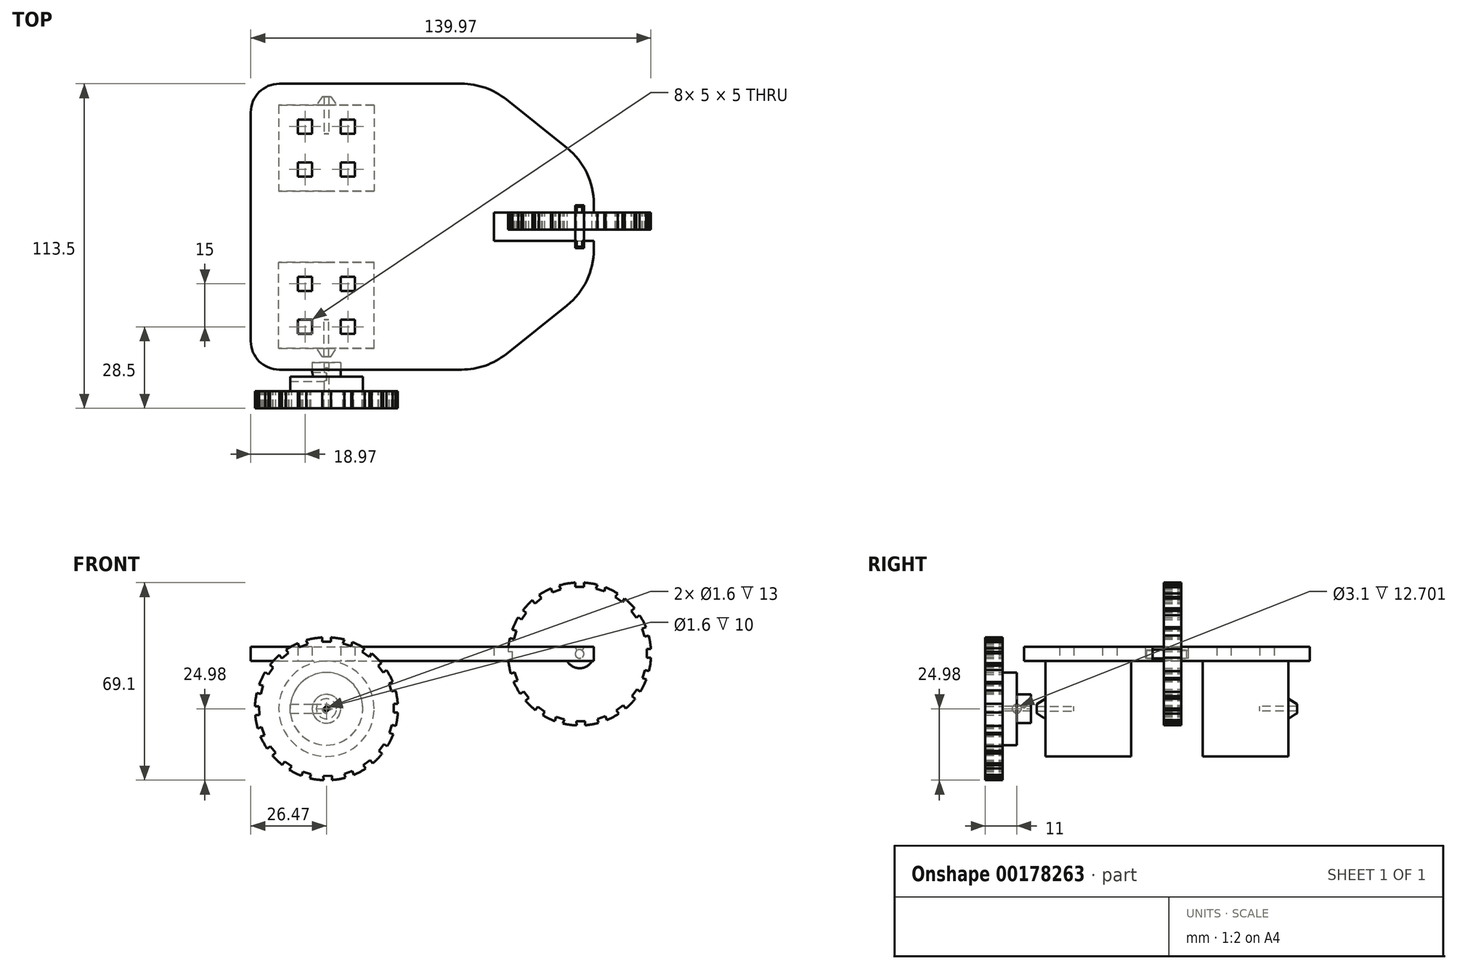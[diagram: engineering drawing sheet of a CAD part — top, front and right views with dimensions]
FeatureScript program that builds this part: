
annotation { "Feature Type Name" : "Feature", "Feature Type Description" : "" }
export const myFeature = defineFeature(function(context is Context, id is Id, definition is map)
    precondition{}
    {
        {
            var Q0;
            Q0=qCreatedBy(makeId("Front.planeOp"),FACE);
            var sketch = newSketch(context, id + "F0", { "sketchPlane" : qUnion([Q0])});
            skCircle(sketch, "E0", {"center": v(0, 0) * mm, "radius": 16.67 * mm});
            skCircle(sketch, "E1", {"center": v(0, 0) * mm, "radius": 0.8 * mm});
            skSolve(sketch);
        }
        {
            var Q0;
            Q0=makeQuery(id+"F0.imprint","IMPRINT",FACE,{"disambiguationData":[TD([[makeQuery(id+"F0.imprint","IMPRINT",EDGE,{"derivedFrom":sQuery(id+"F0.wireOp",EDGE,"E0")}),1.0]])]});
            var Q1;
            Q1=sQuery(id+"F0.wireOp",EDGE,"E0");
            extrude(context, id + "F1", {"entities" : qUnion([Q0]), "surfaceEntities" : qUnion([Q1]), "depth" : 30 * mm});
        }
        {
            var Q0;
            Q0=makeQuery(id+"F0.imprint","IMPRINT",FACE,{"disambiguationData":[TD([[makeQuery(id+"F0.imprint","IMPRINT",EDGE,{"derivedFrom":sQuery(id+"F0.wireOp",EDGE,"E1")}),1.0]])]});
            var Q1;
            Q1=sQuery(id+"F0.wireOp",EDGE,"E1");
            extrude(context, id + "F2", {"entities" : qUnion([Q0]), "surfaceEntities" : qUnion([Q1]), "depth" : 45 * mm});
        }
        {
            var Q0;
            Q0=qCreatedBy(makeId("Front.planeOp"),FACE);
            cPlane(context, id + "F3", {"entities" : qUnion([Q0]), "cplaneType" : CPlaneType.OFFSET, "offset" : 30 * mm, "width" : 150 * mm, "height" : 150 * mm});
        }
        {
            var Q0;
            Q0=qCreatedBy(id+"F3.planeOp",FACE);
            var sketch = newSketch(context, id + "F4", { "sketchPlane" : qUnion([Q0])});
            skCircle(sketch, "E2", {"center": v(0, 0) * mm, "radius": 3.5 * mm});
            skSolve(sketch);
        }
        {
            var Q0;
            Q0 = qSketchRegion(id + "F4", true);
            extrude(context, id + "F5", {"entities" : qUnion([Q0]), "operationType" : NewBodyOperationType.ADD, "depth" : 3 * mm, "hasDraft" : true, "draftAngle" : 33 * degree, "draftPullDirection" : true});
        }
        {
            var Q0;
            Q0=qCreatedBy(makeId("Front.planeOp"),FACE);
            cPlane(context, id + "F6", {"entities" : qUnion([Q0]), "cplaneType" : CPlaneType.OFFSET, "offset" : 45 * mm, "width" : 150 * mm, "height" : 150 * mm});
        }
        {
            var Q0;
            Q0=qCreatedBy(id+"F6.planeOp",FACE);
            var sketch = newSketch(context, id + "F7", { "sketchPlane" : qUnion([Q0])});
            skCircle(sketch, "E3", {"center": v(0, 0) * mm, "radius": 12.7 * mm});
            skCircle(sketch, "E4", {"center": v(0, 0) * mm, "radius": 2.75 * mm});
            skCircle(sketch, "E5", {"center": v(0, 0) * mm, "radius": 0.8 * mm});
            skSolve(sketch);
        }
        {
            var Q0;
            Q0=makeQuery(id+"F7.imprint","IMPRINT",FACE,{"disambiguationData":[TD([[makeQuery(id+"F7.imprint","IMPRINT",EDGE,{"derivedFrom":sQuery(id+"F7.wireOp",EDGE,"E4")}),1.0]])]});
            extrude(context, id + "F8", {"entities" : qUnion([Q0]), "oppositeDirection" : true, "depth" : 10 * mm});
        }
        {
            var Q0;
            Q0 = qSketchRegion(id + "F7", true);
            extrude(context, id + "F9", {"entities" : qUnion([Q0]), "operationType" : NewBodyOperationType.ADD, "oppositeDirection" : true, "depth" : 5 * mm});
        }
        {
            var Q0;
            Q0=makeQuery(id+"F7.imprint","IMPRINT",FACE,{"disambiguationData":[TD([[makeQuery(id+"F7.imprint","IMPRINT",EDGE,{"derivedFrom":sQuery(id+"F7.wireOp",EDGE,"E5")}),1.0]])]});
            var Q1;
            Q1=sQuery(id+"F7.wireOp",EDGE,"E5");
            extrude(context, id + "F10", {"entities" : qUnion([Q0]), "operationType" : NewBodyOperationType.REMOVE, "surfaceEntities" : qUnion([Q1]), "depth" : 25 * mm, "hasSecondDirection" : true, "secondDirectionOppositeDirection" : true, "secondDirectionDepth" : 25 * mm});
        }
        {
            var Q0;
            Q0=qCreatedBy(makeId("Top.planeOp"),FACE);
            var sketch = newSketch(context, id + "F11", { "sketchPlane" : qUnion([Q0])});
            skLineSegment(sketch, "E6", {"start": v(0, 0) * mm, "end": v(0, -37.5) * mm});
            skLineSegment(sketch, "E7", {"start": v(19.12, -37.5) * mm, "end": v(-21.18, -37.5) * mm});
            skCircle(sketch, "E8", {"center": v(0, -37.5) * mm, "radius": 0.75 * mm});
            skSolve(sketch);
        }
        {
            var Q0;
            Q0 = qSketchRegion(id + "F11", true);
            extrude(context, id + "F12", {"entities" : qUnion([Q0]), "operationType" : NewBodyOperationType.REMOVE, "depth" : 25 * mm});
        }
        {
            var Q0;
            Q0=qCreatedBy(id+"F6.planeOp",FACE);
            var sketch = newSketch(context, id + "F13", { "sketchPlane" : qUnion([Q0])});
            skCircle(sketch, "E9", {"center": v(0, 0) * mm, "radius": 25 * mm});
            skLineSegment(sketch, "E10.bottom", {"start": v(0, 25) * mm, "end": v(1.5, 25) * mm});
            skLineSegment(sketch, "E10.top", {"start": v(0, 23.5) * mm, "end": v(1.5, 23.5) * mm});
            skLineSegment(sketch, "E10.right", {"start": v(1.5, 25) * mm, "end": v(1.5, 23.5) * mm});
            skLineSegment(sketch, "E11.MirrorCS", {"start": v(0, 25) * mm, "end": v(-1.5, 25) * mm});
            skLineSegment(sketch, "E12.MirrorCS", {"start": v(-1.5, 25) * mm, "end": v(-1.5, 23.5) * mm});
            skLineSegment(sketch, "E13.MirrorCS", {"start": v(0, 23.5) * mm, "end": v(-1.5, 23.5) * mm});
            skLineSegment(sketch, "E14.1.0", {"start": v(6.25, 24.25) * mm, "end": v(5.8, 22.82) * mm});
            skLineSegment(sketch, "E14.1.1", {"start": v(7.68, 23.8) * mm, "end": v(6.25, 24.25) * mm});
            skLineSegment(sketch, "E14.1.2", {"start": v(7.68, 23.8) * mm, "end": v(9.1, 23.33) * mm});
            skLineSegment(sketch, "E14.1.3", {"start": v(9.1, 23.33) * mm, "end": v(8.65, 21.9) * mm});
            skLineSegment(sketch, "E14.1.4", {"start": v(7.22, 22.36) * mm, "end": v(8.65, 21.9) * mm});
            skLineSegment(sketch, "E14.1.5", {"start": v(7.22, 22.36) * mm, "end": v(5.8, 22.82) * mm});
            skLineSegment(sketch, "E14.2.0", {"start": v(13.4, 21.16) * mm, "end": v(12.53, 19.94) * mm});
            skLineSegment(sketch, "E14.2.1", {"start": v(14.62, 20.28) * mm, "end": v(13.4, 21.16) * mm});
            skLineSegment(sketch, "E14.2.2", {"start": v(14.62, 20.28) * mm, "end": v(15.84, 19.4) * mm});
            skLineSegment(sketch, "E14.2.3", {"start": v(15.84, 19.4) * mm, "end": v(14.96, 18.19) * mm});
            skLineSegment(sketch, "E14.2.4", {"start": v(13.74, 19.06) * mm, "end": v(14.96, 18.19) * mm});
            skLineSegment(sketch, "E14.2.5", {"start": v(13.74, 19.06) * mm, "end": v(12.53, 19.94) * mm});
            skLineSegment(sketch, "E14.3.0", {"start": v(19.26, 16.01) * mm, "end": v(18.05, 15.13) * mm});
            skLineSegment(sketch, "E14.3.1", {"start": v(20.14, 14.8) * mm, "end": v(19.26, 16.01) * mm});
            skLineSegment(sketch, "E14.3.2", {"start": v(20.14, 14.8) * mm, "end": v(21.03, 13.6) * mm});
            skLineSegment(sketch, "E14.3.3", {"start": v(21.03, 13.6) * mm, "end": v(19.82, 12.7) * mm});
            skLineSegment(sketch, "E14.3.4", {"start": v(18.94, 13.92) * mm, "end": v(19.82, 12.7) * mm});
            skLineSegment(sketch, "E14.3.5", {"start": v(18.94, 13.92) * mm, "end": v(18.05, 15.13) * mm});
            skLineSegment(sketch, "E14.4.0", {"start": v(23.25, 9.32) * mm, "end": v(21.82, 8.85) * mm});
            skLineSegment(sketch, "E14.4.1", {"start": v(23.72, 7.9) * mm, "end": v(23.25, 9.32) * mm});
            skLineSegment(sketch, "E14.4.2", {"start": v(23.72, 7.9) * mm, "end": v(24.2, 6.48) * mm});
            skLineSegment(sketch, "E14.4.3", {"start": v(24.2, 6.48) * mm, "end": v(22.77, 6) * mm});
            skLineSegment(sketch, "E14.4.4", {"start": v(22.3, 7.43) * mm, "end": v(22.77, 6) * mm});
            skLineSegment(sketch, "E14.4.5", {"start": v(22.3, 7.43) * mm, "end": v(21.82, 8.85) * mm});
            skLineSegment(sketch, "E14.5.0", {"start": v(24.99, 1.73) * mm, "end": v(23.49, 1.72) * mm});
            skLineSegment(sketch, "E14.5.1", {"start": v(25, 0.23) * mm, "end": v(24.99, 1.73) * mm});
            skLineSegment(sketch, "E14.5.2", {"start": v(25, 0.23) * mm, "end": v(25.01, -1.27) * mm});
            skLineSegment(sketch, "E14.5.3", {"start": v(25.01, -1.27) * mm, "end": v(23.51, -1.28) * mm});
            skLineSegment(sketch, "E14.5.4", {"start": v(23.5, 0.22) * mm, "end": v(23.51, -1.28) * mm});
            skLineSegment(sketch, "E14.5.5", {"start": v(23.5, 0.22) * mm, "end": v(23.49, 1.72) * mm});
            skLineSegment(sketch, "E14.6.0", {"start": v(24.3, -6.03) * mm, "end": v(22.88, -5.58) * mm});
            skLineSegment(sketch, "E14.6.1", {"start": v(23.86, -7.46) * mm, "end": v(24.3, -6.03) * mm});
            skLineSegment(sketch, "E14.6.2", {"start": v(23.86, -7.46) * mm, "end": v(23.41, -8.9) * mm});
            skLineSegment(sketch, "E14.6.3", {"start": v(23.41, -8.9) * mm, "end": v(21.98, -8.45) * mm});
            skLineSegment(sketch, "E14.6.4", {"start": v(22.43, -7.02) * mm, "end": v(21.98, -8.45) * mm});
            skLineSegment(sketch, "E14.6.5", {"start": v(22.43, -7.02) * mm, "end": v(22.88, -5.58) * mm});
            skLineSegment(sketch, "E14.7.0", {"start": v(21.28, -13.2) * mm, "end": v(20.05, -12.34) * mm});
            skLineSegment(sketch, "E14.7.1", {"start": v(20.41, -14.43) * mm, "end": v(21.28, -13.2) * mm});
            skLineSegment(sketch, "E14.7.2", {"start": v(20.41, -14.43) * mm, "end": v(19.55, -15.66) * mm});
            skLineSegment(sketch, "E14.7.3", {"start": v(19.55, -15.66) * mm, "end": v(18.32, -14.8) * mm});
            skLineSegment(sketch, "E14.7.4", {"start": v(19.19, -13.57) * mm, "end": v(18.32, -14.8) * mm});
            skLineSegment(sketch, "E14.7.5", {"start": v(19.19, -13.57) * mm, "end": v(20.05, -12.34) * mm});
            skLineSegment(sketch, "E14.8.0", {"start": v(16.2, -19.1) * mm, "end": v(15.3, -17.9) * mm});
            skLineSegment(sketch, "E14.8.1", {"start": v(15, -20) * mm, "end": v(16.2, -19.1) * mm});
            skLineSegment(sketch, "E14.8.2", {"start": v(15, -20) * mm, "end": v(13.79, -20.9) * mm});
            skLineSegment(sketch, "E14.8.3", {"start": v(13.79, -20.9) * mm, "end": v(12.9, -19.7) * mm});
            skLineSegment(sketch, "E14.8.4", {"start": v(14.1, -18.8) * mm, "end": v(12.9, -19.7) * mm});
            skLineSegment(sketch, "E14.8.5", {"start": v(14.1, -18.8) * mm, "end": v(15.3, -17.9) * mm});
            skLineSegment(sketch, "E14.9.0", {"start": v(9.54, -23.16) * mm, "end": v(9.05, -21.74) * mm});
            skLineSegment(sketch, "E14.9.1", {"start": v(8.12, -23.65) * mm, "end": v(9.54, -23.16) * mm});
            skLineSegment(sketch, "E14.9.2", {"start": v(8.12, -23.65) * mm, "end": v(6.7, -24.13) * mm});
            skLineSegment(sketch, "E14.9.3", {"start": v(6.7, -24.13) * mm, "end": v(6.21, -22.71) * mm});
            skLineSegment(sketch, "E14.9.4", {"start": v(7.63, -22.23) * mm, "end": v(6.21, -22.71) * mm});
            skLineSegment(sketch, "E14.9.5", {"start": v(7.63, -22.23) * mm, "end": v(9.05, -21.74) * mm});
            skLineSegment(sketch, "E14.10.0", {"start": v(1.96, -24.97) * mm, "end": v(1.93, -23.47) * mm});
            skLineSegment(sketch, "E14.10.1", {"start": v(0.46, -25) * mm, "end": v(1.96, -24.97) * mm});
            skLineSegment(sketch, "E14.10.2", {"start": v(0.46, -25) * mm, "end": v(-1.04, -25.02) * mm});
            skLineSegment(sketch, "E14.10.3", {"start": v(-1.04, -25.02) * mm, "end": v(-1.07, -23.52) * mm});
            skLineSegment(sketch, "E14.10.4", {"start": v(0.43, -23.5) * mm, "end": v(-1.07, -23.52) * mm});
            skLineSegment(sketch, "E14.10.5", {"start": v(0.43, -23.5) * mm, "end": v(1.93, -23.47) * mm});
            skLineSegment(sketch, "E14.11.0", {"start": v(-5.8, -24.36) * mm, "end": v(-5.37, -22.93) * mm});
            skLineSegment(sketch, "E14.11.1", {"start": v(-7.24, -23.93) * mm, "end": v(-5.8, -24.36) * mm});
            skLineSegment(sketch, "E14.11.2", {"start": v(-7.24, -23.93) * mm, "end": v(-8.68, -23.5) * mm});
            skLineSegment(sketch, "E14.11.3", {"start": v(-8.68, -23.5) * mm, "end": v(-8.24, -22.06) * mm});
            skLineSegment(sketch, "E14.11.4", {"start": v(-6.8, -22.5) * mm, "end": v(-8.24, -22.06) * mm});
            skLineSegment(sketch, "E14.11.5", {"start": v(-6.8, -22.5) * mm, "end": v(-5.37, -22.93) * mm});
            skLineSegment(sketch, "E14.12.0", {"start": v(-13.01, -21.4) * mm, "end": v(-12.16, -20.17) * mm});
            skLineSegment(sketch, "E14.12.1", {"start": v(-14.25, -20.54) * mm, "end": v(-13.01, -21.4) * mm});
            skLineSegment(sketch, "E14.12.2", {"start": v(-14.25, -20.54) * mm, "end": v(-15.48, -19.69) * mm});
            skLineSegment(sketch, "E14.12.3", {"start": v(-15.48, -19.69) * mm, "end": v(-14.62, -18.46) * mm});
            skLineSegment(sketch, "E14.12.4", {"start": v(-13.4, -19.31) * mm, "end": v(-14.62, -18.46) * mm});
            skLineSegment(sketch, "E14.12.5", {"start": v(-13.4, -19.31) * mm, "end": v(-12.16, -20.17) * mm});
            skLineSegment(sketch, "E14.13.0", {"start": v(-18.96, -16.37) * mm, "end": v(-17.77, -15.46) * mm});
            skLineSegment(sketch, "E14.13.1", {"start": v(-19.87, -15.17) * mm, "end": v(-18.96, -16.37) * mm});
            skLineSegment(sketch, "E14.13.2", {"start": v(-19.87, -15.17) * mm, "end": v(-20.78, -13.98) * mm});
            skLineSegment(sketch, "E14.13.3", {"start": v(-20.78, -13.98) * mm, "end": v(-19.59, -13.07) * mm});
            skLineSegment(sketch, "E14.13.4", {"start": v(-18.68, -14.26) * mm, "end": v(-19.59, -13.07) * mm});
            skLineSegment(sketch, "E14.13.5", {"start": v(-18.68, -14.26) * mm, "end": v(-17.77, -15.46) * mm});
            skLineSegment(sketch, "E14.14.0", {"start": v(-23.07, -9.75) * mm, "end": v(-21.66, -9.25) * mm});
            skLineSegment(sketch, "E14.14.1", {"start": v(-23.57, -8.33) * mm, "end": v(-23.07, -9.75) * mm});
            skLineSegment(sketch, "E14.14.2", {"start": v(-23.57, -8.33) * mm, "end": v(-24.07, -6.92) * mm});
            skLineSegment(sketch, "E14.14.3", {"start": v(-24.07, -6.92) * mm, "end": v(-22.66, -6.42) * mm});
            skLineSegment(sketch, "E14.14.4", {"start": v(-22.16, -7.83) * mm, "end": v(-22.66, -6.42) * mm});
            skLineSegment(sketch, "E14.14.5", {"start": v(-22.16, -7.83) * mm, "end": v(-21.66, -9.25) * mm});
            skLineSegment(sketch, "E14.15.0", {"start": v(-24.95, -2.19) * mm, "end": v(-23.45, -2.15) * mm});
            skLineSegment(sketch, "E14.15.1", {"start": v(-25, -0.69) * mm, "end": v(-24.95, -2.19) * mm});
            skLineSegment(sketch, "E14.15.2", {"start": v(-25, -0.69) * mm, "end": v(-25.03, 0.81) * mm});
            skLineSegment(sketch, "E14.15.3", {"start": v(-25.03, 0.81) * mm, "end": v(-23.53, 0.85) * mm});
            skLineSegment(sketch, "E14.15.4", {"start": v(-23.5, -0.65) * mm, "end": v(-23.53, 0.85) * mm});
            skLineSegment(sketch, "E14.15.5", {"start": v(-23.5, -0.65) * mm, "end": v(-23.45, -2.15) * mm});
            skLineSegment(sketch, "E14.16.0", {"start": v(-24.41, 5.58) * mm, "end": v(-22.98, 5.16) * mm});
            skLineSegment(sketch, "E14.16.1", {"start": v(-24, 7.02) * mm, "end": v(-24.41, 5.58) * mm});
            skLineSegment(sketch, "E14.16.2", {"start": v(-24, 7.02) * mm, "end": v(-23.57, 8.46) * mm});
            skLineSegment(sketch, "E14.16.3", {"start": v(-23.57, 8.46) * mm, "end": v(-22.13, 8.04) * mm});
            skLineSegment(sketch, "E14.16.4", {"start": v(-22.55, 6.6) * mm, "end": v(-22.13, 8.04) * mm});
            skLineSegment(sketch, "E14.16.5", {"start": v(-22.55, 6.6) * mm, "end": v(-22.98, 5.16) * mm});
            skLineSegment(sketch, "E14.17.0", {"start": v(-21.52, 12.82) * mm, "end": v(-20.28, 11.97) * mm});
            skLineSegment(sketch, "E14.17.1", {"start": v(-20.67, 14.06) * mm, "end": v(-21.52, 12.82) * mm});
            skLineSegment(sketch, "E14.17.2", {"start": v(-20.67, 14.06) * mm, "end": v(-19.83, 15.3) * mm});
            skLineSegment(sketch, "E14.17.3", {"start": v(-19.83, 15.3) * mm, "end": v(-18.6, 14.45) * mm});
            skLineSegment(sketch, "E14.17.4", {"start": v(-19.43, 13.21) * mm, "end": v(-18.6, 14.45) * mm});
            skLineSegment(sketch, "E14.17.5", {"start": v(-19.43, 13.21) * mm, "end": v(-20.28, 11.97) * mm});
            skLineSegment(sketch, "E14.18.0", {"start": v(-16.54, 18.8) * mm, "end": v(-15.62, 17.62) * mm});
            skLineSegment(sketch, "E14.18.1", {"start": v(-15.36, 19.73) * mm, "end": v(-16.54, 18.8) * mm});
            skLineSegment(sketch, "E14.18.2", {"start": v(-15.36, 19.73) * mm, "end": v(-14.17, 20.65) * mm});
            skLineSegment(sketch, "E14.18.3", {"start": v(-14.17, 20.65) * mm, "end": v(-13.25, 19.47) * mm});
            skLineSegment(sketch, "E14.18.4", {"start": v(-14.43, 18.54) * mm, "end": v(-13.25, 19.47) * mm});
            skLineSegment(sketch, "E14.18.5", {"start": v(-14.43, 18.54) * mm, "end": v(-15.62, 17.62) * mm});
            skLineSegment(sketch, "E14.19.0", {"start": v(-9.96, 22.98) * mm, "end": v(-9.45, 21.57) * mm});
            skLineSegment(sketch, "E14.19.1", {"start": v(-8.55, 23.5) * mm, "end": v(-9.96, 22.98) * mm});
            skLineSegment(sketch, "E14.19.2", {"start": v(-8.55, 23.5) * mm, "end": v(-7.14, 24) * mm});
            skLineSegment(sketch, "E14.19.3", {"start": v(-7.14, 24) * mm, "end": v(-6.63, 22.6) * mm});
            skLineSegment(sketch, "E14.19.4", {"start": v(-8.04, 22.08) * mm, "end": v(-6.63, 22.6) * mm});
            skLineSegment(sketch, "E14.19.5", {"start": v(-8.04, 22.08) * mm, "end": v(-9.45, 21.57) * mm});
            skLineSegment(sketch, "E14.anchor1", {"start": v(0, 0) * mm, "end": v(-1.5, 23.5) * mm, "construction": true});
            skLineSegment(sketch, "E14.anchor2", {"start": v(0, 0) * mm, "end": v(-9.45, 21.57) * mm, "construction": true});
            skCircle(sketch, "E15", {"center": v(0, 0) * mm, "radius": 0.82 * mm});
            skCircle(sketch, "E16", {"center": v(0, 0) * mm, "radius": 5 * mm});
            skSolve(sketch);
        }
        {
            var Q0;
            {var subQ37=sQuery(id+"F13.wireOp",EDGE,"E10.top");Q0=makeQuery(id+"F13.imprint","IMPRINT",FACE,{"disambiguationData":[TD([[makeQuery(id+"F13.imprint","IMPRINT",EDGE,{"derivedFrom":subQ37}),-1.0]])]});}
            var Q1;
            Q1=makeQuery(id+"F13.imprint","IMPRINT",FACE,{"disambiguationData":[TD([[makeQuery(id+"F13.imprint","IMPRINT",EDGE,{"derivedFrom":sQuery(id+"F13.wireOp",EDGE,"E15")}),-1.0]])]});
            extrude(context, id + "F14", {"entities" : qUnion([Q0, Q1]), "operationType" : NewBodyOperationType.ADD, "depth" : 6 * mm});
        }
        {
            var Q0;
            Q0=makeQuery(id+"F13.imprint","IMPRINT",FACE,{"disambiguationData":[TD([[makeQuery(id+"F13.imprint","IMPRINT",EDGE,{"derivedFrom":sQuery(id+"F13.wireOp",EDGE,"E15")}),-1.0]])]});
            extrude(context, id + "F15", {"entities" : qUnion([Q0]), "operationType" : NewBodyOperationType.ADD, "oppositeDirection" : true, "depth" : 10 * mm});
        }
        {
            var Q0;
            Q0=qCreatedBy(makeId("Right.planeOp"),FACE);
            var sketch = newSketch(context, id + "F16", { "sketchPlane" : qUnion([Q0])});
            skLineSegment(sketch, "E17", {"start": v(-35, 0) * mm, "end": v(-35, 17.32) * mm});
            skLineSegment(sketch, "E18.0", {"start": v(-40, 0) * mm, "end": v(-40, 17.32) * mm});
            skCircle(sketch, "E19", {"center": v(-40, 0) * mm, "radius": 1.55 * mm});
            skSolve(sketch);
        }
        {
            var Q0;
            Q0=makeQuery(id+"F16.imprint","IMPRINT",FACE,{"disambiguationData":[TD([[makeQuery(id+"F16.imprint","IMPRINT",EDGE,{"derivedFrom":sQuery(id+"F16.wireOp",EDGE,"E19")}),1.0]])]});
            extrude(context, id + "F17", {"entities" : qUnion([Q0]), "operationType" : NewBodyOperationType.REMOVE, "oppositeDirection" : true, "depth" : 25 * mm});
        }
        {
            var Q0;
            Q0=qCreatedBy(makeId("Front.planeOp"),FACE);
            cPlane(context, id + "F18", {"entities" : qUnion([Q0]), "cplaneType" : CPlaneType.OFFSET, "offset" : 12.5 * mm, "oppositeDirection" : true, "width" : 150 * mm, "height" : 150 * mm});
        }
        {
            var Q0;
            Q0=makeQuery(id+"F1.opExtrude","SWEPT_BODY",BODY,{"disambiguationData":[OSD([sQuery(id+"F0.wireOp",EDGE,"E0"),sQuery(id+"F0.wireOp",EDGE,"E1")])]});
            var Q1;
            Q1=makeQuery(id+"F14.opExtrude","SWEPT_BODY",BODY,{"disambiguationData":[OSD([sQuery(id+"F13.wireOp",EDGE,"E9"),sQuery(id+"F13.wireOp",EDGE,"E10.top"),sQuery(id+"F13.wireOp",EDGE,"E10.right"),sQuery(id+"F13.wireOp",EDGE,"E12.MirrorCS"),sQuery(id+"F13.wireOp",EDGE,"E13.MirrorCS"),sQuery(id+"F13.wireOp",EDGE,"E14.1.0"),sQuery(id+"F13.wireOp",EDGE,"E14.1.3"),sQuery(id+"F13.wireOp",EDGE,"E14.1.4"),sQuery(id+"F13.wireOp",EDGE,"E14.1.5"),sQuery(id+"F13.wireOp",EDGE,"E14.2.0"),sQuery(id+"F13.wireOp",EDGE,"E14.2.3"),sQuery(id+"F13.wireOp",EDGE,"E14.2.4"),sQuery(id+"F13.wireOp",EDGE,"E14.2.5"),sQuery(id+"F13.wireOp",EDGE,"E14.3.0"),sQuery(id+"F13.wireOp",EDGE,"E14.3.3"),sQuery(id+"F13.wireOp",EDGE,"E14.3.4"),sQuery(id+"F13.wireOp",EDGE,"E14.3.5"),sQuery(id+"F13.wireOp",EDGE,"E14.4.0"),sQuery(id+"F13.wireOp",EDGE,"E14.4.3"),sQuery(id+"F13.wireOp",EDGE,"E14.4.4"),sQuery(id+"F13.wireOp",EDGE,"E14.4.5"),sQuery(id+"F13.wireOp",EDGE,"E14.5.0"),sQuery(id+"F13.wireOp",EDGE,"E14.5.3"),sQuery(id+"F13.wireOp",EDGE,"E14.5.4"),sQuery(id+"F13.wireOp",EDGE,"E14.5.5"),sQuery(id+"F13.wireOp",EDGE,"E14.6.0"),sQuery(id+"F13.wireOp",EDGE,"E14.6.3"),sQuery(id+"F13.wireOp",EDGE,"E14.6.4"),sQuery(id+"F13.wireOp",EDGE,"E14.6.5"),sQuery(id+"F13.wireOp",EDGE,"E14.7.0"),sQuery(id+"F13.wireOp",EDGE,"E14.7.3"),sQuery(id+"F13.wireOp",EDGE,"E14.7.4"),sQuery(id+"F13.wireOp",EDGE,"E14.7.5"),sQuery(id+"F13.wireOp",EDGE,"E14.8.0"),sQuery(id+"F13.wireOp",EDGE,"E14.8.3"),sQuery(id+"F13.wireOp",EDGE,"E14.8.4"),sQuery(id+"F13.wireOp",EDGE,"E14.8.5"),sQuery(id+"F13.wireOp",EDGE,"E14.9.0"),sQuery(id+"F13.wireOp",EDGE,"E14.9.3"),sQuery(id+"F13.wireOp",EDGE,"E14.9.4"),sQuery(id+"F13.wireOp",EDGE,"E14.9.5"),sQuery(id+"F13.wireOp",EDGE,"E14.10.0"),sQuery(id+"F13.wireOp",EDGE,"E14.10.3"),sQuery(id+"F13.wireOp",EDGE,"E14.10.4"),sQuery(id+"F13.wireOp",EDGE,"E14.10.5"),sQuery(id+"F13.wireOp",EDGE,"E14.11.0"),sQuery(id+"F13.wireOp",EDGE,"E14.11.3"),sQuery(id+"F13.wireOp",EDGE,"E14.11.4"),sQuery(id+"F13.wireOp",EDGE,"E14.11.5"),sQuery(id+"F13.wireOp",EDGE,"E14.12.0"),sQuery(id+"F13.wireOp",EDGE,"E14.12.3"),sQuery(id+"F13.wireOp",EDGE,"E14.12.4"),sQuery(id+"F13.wireOp",EDGE,"E14.12.5"),sQuery(id+"F13.wireOp",EDGE,"E14.13.0"),sQuery(id+"F13.wireOp",EDGE,"E14.13.3"),sQuery(id+"F13.wireOp",EDGE,"E14.13.4"),sQuery(id+"F13.wireOp",EDGE,"E14.13.5"),sQuery(id+"F13.wireOp",EDGE,"E14.14.0"),sQuery(id+"F13.wireOp",EDGE,"E14.14.3"),sQuery(id+"F13.wireOp",EDGE,"E14.14.4"),sQuery(id+"F13.wireOp",EDGE,"E14.14.5"),sQuery(id+"F13.wireOp",EDGE,"E14.15.0"),sQuery(id+"F13.wireOp",EDGE,"E14.15.3"),sQuery(id+"F13.wireOp",EDGE,"E14.15.4"),sQuery(id+"F13.wireOp",EDGE,"E14.15.5"),sQuery(id+"F13.wireOp",EDGE,"E14.16.0"),sQuery(id+"F13.wireOp",EDGE,"E14.16.3"),sQuery(id+"F13.wireOp",EDGE,"E14.16.4"),sQuery(id+"F13.wireOp",EDGE,"E14.16.5"),sQuery(id+"F13.wireOp",EDGE,"E14.17.0"),sQuery(id+"F13.wireOp",EDGE,"E14.17.3"),sQuery(id+"F13.wireOp",EDGE,"E14.17.4"),sQuery(id+"F13.wireOp",EDGE,"E14.17.5"),sQuery(id+"F13.wireOp",EDGE,"E14.18.0"),sQuery(id+"F13.wireOp",EDGE,"E14.18.3"),sQuery(id+"F13.wireOp",EDGE,"E14.18.4"),sQuery(id+"F13.wireOp",EDGE,"E14.18.5"),sQuery(id+"F13.wireOp",EDGE,"E14.19.0"),sQuery(id+"F13.wireOp",EDGE,"E14.19.3"),sQuery(id+"F13.wireOp",EDGE,"E14.19.4"),sQuery(id+"F13.wireOp",EDGE,"E14.19.5"),sQuery(id+"F13.wireOp",EDGE,"E15")])]});
            var Q2;
            Q2=makeQuery(id+"F2.opExtrude","SWEPT_BODY",BODY,{"disambiguationData":[OSD([sQuery(id+"F0.wireOp",EDGE,"E1")])]});
            var Q3;
            Q3=qCreatedBy(id+"F18.planeOp",FACE);
            mirror(context, id + "F19", {"entities" : qUnion([Q0, Q1, Q2]), "mirrorPlane" : qUnion([Q3])});
        }
        {
            var Q0;
            Q0=qCreatedBy(makeId("Top.planeOp"),FACE);
            cPlane(context, id + "F20", {"entities" : qUnion([Q0]), "cplaneType" : CPlaneType.OFFSET, "offset" : 16.67 * mm, "width" : 150 * mm, "height" : 150 * mm});
        }
        {
            var Q0;
            Q0=qCreatedBy(id+"F20.planeOp",FACE);
            var sketch = newSketch(context, id + "F21", { "sketchPlane" : qUnion([Q0])});
            skLineSegment(sketch, "E20.0", {"start": v(-26.47, -27.5) * mm, "end": v(-26.47, 52.5) * mm});
            skLineSegment(sketch, "E21.0", {"start": v(-16.47, 62.5) * mm, "end": v(47.26, 62.5) * mm});
            skLineSegment(sketch, "E22.MirrorCS", {"start": v(-16.47, -37.5) * mm, "end": v(47.26, -37.5) * mm});
            skLineSegment(sketch, "E23", {"start": v(93.53, 17.5) * mm, "end": v(93.53, 20.48) * mm});
            skLineSegment(sketch, "E24.MirrorCS", {"start": v(93.53, 7.5) * mm, "end": v(93.53, 4.52) * mm});
            skLineSegment(sketch, "E25", {"start": v(62.88, -32.02) * mm, "end": v(84.15, -15) * mm});
            skLineSegment(sketch, "E26.MirrorCS", {"start": v(62.88, 57.02) * mm, "end": v(84.15, 40) * mm});
            skPoint(sketch, "E27.visualSharp", {"position": v(-26.47, -37.5) * mm});
            skArc(sketch, "E27.filletArc", {"start": v(-26.47, -27.5) * mm, "mid": v(-23.54, -34.57) * mm, "end": v(-16.47, -37.5) * mm});
            skPoint(sketch, "E28.visualSharp", {"position": v(-26.47, 62.5) * mm});
            skArc(sketch, "E28.filletArc", {"start": v(-16.47, 62.5) * mm, "mid": v(-23.54, 59.57) * mm, "end": v(-26.47, 52.5) * mm});
            skLineSegment(sketch, "E29", {"start": v(0, 0) * mm, "end": v(0, 25) * mm});
            skPoint(sketch, "E30.visualSharp", {"position": v(56.03, -37.5) * mm});
            skArc(sketch, "E30.filletArc", {"start": v(47.26, -37.5) * mm, "mid": v(55.54, -36.1) * mm, "end": v(62.88, -32.02) * mm});
            skPoint(sketch, "E31.visualSharp", {"position": v(93.53, -7.5) * mm});
            skArc(sketch, "E31.filletArc", {"start": v(84.15, -15) * mm, "mid": v(91.07, -6.31) * mm, "end": v(93.53, 4.52) * mm});
            skPoint(sketch, "E32.visualSharp", {"position": v(93.53, 32.5) * mm});
            skArc(sketch, "E32.filletArc", {"start": v(93.53, 20.48) * mm, "mid": v(91.07, 31.31) * mm, "end": v(84.15, 40) * mm});
            skPoint(sketch, "E33.visualSharp", {"position": v(56.03, 62.5) * mm});
            skArc(sketch, "E33.filletArc", {"start": v(62.88, 57.02) * mm, "mid": v(55.54, 61.1) * mm, "end": v(47.26, 62.5) * mm});
            skLineSegment(sketch, "E34", {"start": v(93.53, 12.5) * mm, "end": v(58.53, 12.5) * mm});
            skLineSegment(sketch, "E35.0", {"start": v(93.53, 17.5) * mm, "end": v(58.53, 17.5) * mm});
            skLineSegment(sketch, "E36.MirrorCS", {"start": v(93.53, 7.5) * mm, "end": v(58.53, 7.5) * mm});
            skLineSegment(sketch, "E37", {"start": v(58.53, 17.5) * mm, "end": v(58.53, 7.5) * mm});
            skLineSegment(sketch, "E38", {"start": v(5, 25) * mm, "end": v(-5, 25) * mm});
            skLineSegment(sketch, "E39", {"start": v(-5, 45) * mm, "end": v(-5, 50) * mm});
            skLineSegment(sketch, "E40.0", {"start": v(-10, 45) * mm, "end": v(-10, 50) * mm});
            skLineSegment(sketch, "E41", {"start": v(-5, 50) * mm, "end": v(-10, 50) * mm});
            skLineSegment(sketch, "E42", {"start": v(-10, 45) * mm, "end": v(-5, 45) * mm});
            skLineSegment(sketch, "E43", {"start": v(-5, 35) * mm, "end": v(-5, 30) * mm});
            skLineSegment(sketch, "E44.0", {"start": v(-10, 35) * mm, "end": v(-10, 30) * mm});
            skLineSegment(sketch, "E45", {"start": v(-10, 35) * mm, "end": v(-5, 35) * mm});
            skLineSegment(sketch, "E46", {"start": v(-10, 30) * mm, "end": v(-5, 30) * mm});
            skLineSegment(sketch, "E47", {"start": v(5, 50) * mm, "end": v(5, 45) * mm});
            skLineSegment(sketch, "E48", {"start": v(5, 35) * mm, "end": v(5, 30) * mm});
            skLineSegment(sketch, "E49.0", {"start": v(10, 50) * mm, "end": v(10, 45) * mm});
            skLineSegment(sketch, "E50.0", {"start": v(10, 35) * mm, "end": v(10, 30) * mm});
            skLineSegment(sketch, "E51", {"start": v(10, 35) * mm, "end": v(5, 35) * mm});
            skLineSegment(sketch, "E52", {"start": v(10, 30) * mm, "end": v(5, 30) * mm});
            skLineSegment(sketch, "E53", {"start": v(10, 45) * mm, "end": v(5, 45) * mm});
            skLineSegment(sketch, "E54", {"start": v(10, 50) * mm, "end": v(5, 50) * mm});
            skLineSegment(sketch, "E55.MirrorCS", {"start": v(10, -25) * mm, "end": v(10, -20) * mm});
            skLineSegment(sketch, "E56.MirrorCS", {"start": v(-10, -20) * mm, "end": v(-10, -25) * mm});
            skLineSegment(sketch, "E57.MirrorCS", {"start": v(10, -20) * mm, "end": v(5, -20) * mm});
            skLineSegment(sketch, "E58.MirrorCS", {"start": v(5, -25) * mm, "end": v(5, -20) * mm});
            skLineSegment(sketch, "E59.MirrorCS", {"start": v(10, -5) * mm, "end": v(5, -5) * mm});
            skLineSegment(sketch, "E60.MirrorCS", {"start": v(-10, -10) * mm, "end": v(-5, -10) * mm});
            skLineSegment(sketch, "E61.MirrorCS", {"start": v(-5, -10) * mm, "end": v(-5, -5) * mm});
            skLineSegment(sketch, "E62.MirrorCS", {"start": v(10, -10) * mm, "end": v(5, -10) * mm});
            skLineSegment(sketch, "E63.MirrorCS", {"start": v(-10, -5) * mm, "end": v(-5, -5) * mm});
            skLineSegment(sketch, "E64.MirrorCS", {"start": v(-10, -20) * mm, "end": v(-5, -20) * mm});
            skLineSegment(sketch, "E65.MirrorCS", {"start": v(-5, -25) * mm, "end": v(-10, -25) * mm});
            skLineSegment(sketch, "E66.MirrorCS", {"start": v(-5, -20) * mm, "end": v(-5, -25) * mm});
            skLineSegment(sketch, "E67.MirrorCS", {"start": v(5, -10) * mm, "end": v(5, -5) * mm});
            skLineSegment(sketch, "E68.MirrorCS", {"start": v(10, -10) * mm, "end": v(10, -5) * mm});
            skLineSegment(sketch, "E69.MirrorCS", {"start": v(-10, -10) * mm, "end": v(-10, -5) * mm});
            skLineSegment(sketch, "E70.MirrorCS", {"start": v(10, -25) * mm, "end": v(5, -25) * mm});
            skSolve(sketch);
        }
        {
            var Q0;
            Q0 = qSketchRegion(id + "F21", true);
            extrude(context, id + "F22", {"entities" : qUnion([Q0]), "depth" : 5 * mm});
        }
        {
            var Q0;
            Q0=makeQuery(id+"F22.opExtrude","SWEPT_FACE",FACE,{"disambiguationData":[OSD([sQuery(id+"F21.wireOp",EDGE,"E35.0")])]});
            var sketch = newSketch(context, id + "F23", { "sketchPlane" : qUnion([Q0])});
            skLineSegment(sketch, "E71", {"start": v(93.53, 21.67) * mm, "end": v(93.53, 16.67) * mm});
            skLineSegment(sketch, "E72.0", {"start": v(88.53, 21.67) * mm, "end": v(88.53, 16.67) * mm});
            skLineSegment(sketch, "E73.0", {"start": v(93.53, 19.17) * mm, "end": v(88.53, 19.17) * mm});
            skArc(sketch, "E74", {"start": v(87.57, 20.32) * mm, "mid": v(88.53, 17.67) * mm, "end": v(89.5, 20.32) * mm});
            skLineSegment(sketch, "E75", {"start": v(90.03, 21.67) * mm, "end": v(89.5, 20.32) * mm});
            skLineSegment(sketch, "E76.MirrorCS", {"start": v(87.03, 21.67) * mm, "end": v(87.57, 20.32) * mm});
            skLineSegment(sketch, "E77", {"start": v(87.03, 21.67) * mm, "end": v(90.03, 21.67) * mm});
            skSolve(sketch);
        }
        {
            var Q0;
            {var subQ0=sQuery(id+"F23.wireOp",EDGE,"E75");Q0=makeQuery(id+"F23.imprint","IMPRINT",FACE,{"disambiguationData":[TD([[makeQuery(id+"F23.imprint","IMPRINT",EDGE,{"derivedFrom":subQ0}),-1.0]])]});}
            var Q1;
            {var subQ0=sQuery(id+"F23.wireOp",EDGE,"E73.0");var subQ1=sQuery(id+"F23.wireOp",EDGE,"E72.0");var subQ2=makeQuery(id+"F23.imprint","INTERSECT",VERTEX,{"derivedFrom":[subQ1,subQ0]});Q1=makeQuery(id+"F23.imprint","IMPRINT",FACE,{"disambiguationData":[TD([[makeQuery(id+"F23.imprint","IMPRINT",EDGE,{"disambiguationData":[TD([[subQ2,-1.0]])],"derivedFrom":subQ1}),1.0]])]});}
            var Q2;
            {var subQ0=sQuery(id+"F23.wireOp",EDGE,"E76.MirrorCS");Q2=makeQuery(id+"F23.imprint","IMPRINT",FACE,{"disambiguationData":[TD([[makeQuery(id+"F23.imprint","IMPRINT",EDGE,{"derivedFrom":subQ0}),1.0]])]});}
            extrude(context, id + "F24", {"entities" : qUnion([Q0, Q1, Q2]), "operationType" : NewBodyOperationType.REMOVE, "oppositeDirection" : true, "depth" : 2.5 * mm, "hasSecondDirection" : true, "secondDirectionOppositeDirection" : false, "secondDirectionDepth" : 12.5 * mm});
        }
        {
            var Q0;
            Q0=makeQuery(id+"F22.opExtrude","SWEPT_FACE",FACE,{"disambiguationData":[OSD([sQuery(id+"F21.wireOp",EDGE,"E35.0")])]});
            var sketch = newSketch(context, id + "F25", { "sketchPlane" : qUnion([Q0])});
            skCircle(sketch, "E78", {"center": v(88.53, 19.17) * mm, "radius": 1.5 * mm});
            skSolve(sketch);
        }
        {
            var Q0;
            Q0 = qSketchRegion(id + "F25", true);
            extrude(context, id + "F26", {"entities" : qUnion([Q0]), "depth" : 12 * mm, "hasSecondDirection" : true, "secondDirectionOppositeDirection" : true, "secondDirectionDepth" : 2 * mm});
        }
        {
            var Q0;
            Q0=makeQuery(id+"F22.opExtrude","SWEPT_FACE",FACE,{"disambiguationData":[OSD([sQuery(id+"F21.wireOp",EDGE,"E35.0")])]});
            var sketch = newSketch(context, id + "F27", { "sketchPlane" : qUnion([Q0])});
            skCircle(sketch, "E79", {"center": v(88.53, 19.17) * mm, "radius": 25 * mm});
            skLineSegment(sketch, "E80.bottom", {"start": v(88.53, 44.17) * mm, "end": v(90.03, 44.17) * mm});
            skLineSegment(sketch, "E80.top", {"start": v(88.53, 42.67) * mm, "end": v(90.03, 42.67) * mm});
            skLineSegment(sketch, "E80.right", {"start": v(90.03, 44.17) * mm, "end": v(90.03, 42.67) * mm});
            skLineSegment(sketch, "E81.MirrorCS", {"start": v(88.53, 44.17) * mm, "end": v(87.03, 44.17) * mm});
            skLineSegment(sketch, "E82.MirrorCS", {"start": v(87.03, 44.17) * mm, "end": v(87.03, 42.67) * mm});
            skLineSegment(sketch, "E83.MirrorCS", {"start": v(88.53, 42.67) * mm, "end": v(87.03, 42.67) * mm});
            skLineSegment(sketch, "E84.1.0", {"start": v(94.79, 43.42) * mm, "end": v(94.33, 42) * mm});
            skLineSegment(sketch, "E84.1.1", {"start": v(96.22, 42.96) * mm, "end": v(94.79, 43.42) * mm});
            skLineSegment(sketch, "E84.1.2", {"start": v(96.22, 42.96) * mm, "end": v(97.64, 42.5) * mm});
            skLineSegment(sketch, "E84.1.3", {"start": v(97.64, 42.5) * mm, "end": v(97.18, 41.07) * mm});
            skLineSegment(sketch, "E84.1.4", {"start": v(95.75, 41.53) * mm, "end": v(97.18, 41.07) * mm});
            skLineSegment(sketch, "E84.1.5", {"start": v(95.75, 41.53) * mm, "end": v(94.33, 42) * mm});
            skLineSegment(sketch, "E84.2.0", {"start": v(101.94, 40.33) * mm, "end": v(101.06, 39.1) * mm});
            skLineSegment(sketch, "E84.2.1", {"start": v(103.15, 39.45) * mm, "end": v(101.94, 40.33) * mm});
            skLineSegment(sketch, "E84.2.2", {"start": v(103.15, 39.45) * mm, "end": v(104.37, 38.57) * mm});
            skLineSegment(sketch, "E84.2.3", {"start": v(104.37, 38.57) * mm, "end": v(103.5, 37.36) * mm});
            skLineSegment(sketch, "E84.2.4", {"start": v(102.28, 38.23) * mm, "end": v(103.5, 37.36) * mm});
            skLineSegment(sketch, "E84.2.5", {"start": v(102.28, 38.23) * mm, "end": v(101.06, 39.1) * mm});
            skLineSegment(sketch, "E84.3.0", {"start": v(107.79, 35.18) * mm, "end": v(106.58, 34.3) * mm});
            skLineSegment(sketch, "E84.3.1", {"start": v(108.68, 33.98) * mm, "end": v(107.79, 35.18) * mm});
            skLineSegment(sketch, "E84.3.2", {"start": v(108.68, 33.98) * mm, "end": v(109.57, 32.77) * mm});
            skLineSegment(sketch, "E84.3.3", {"start": v(109.57, 32.77) * mm, "end": v(108.36, 31.88) * mm});
            skLineSegment(sketch, "E84.3.4", {"start": v(107.47, 33.09) * mm, "end": v(108.36, 31.88) * mm});
            skLineSegment(sketch, "E84.3.5", {"start": v(107.47, 33.09) * mm, "end": v(106.58, 34.3) * mm});
            skLineSegment(sketch, "E84.4.0", {"start": v(111.78, 28.5) * mm, "end": v(110.36, 28.02) * mm});
            skLineSegment(sketch, "E84.4.1", {"start": v(112.25, 27.07) * mm, "end": v(111.78, 28.5) * mm});
            skLineSegment(sketch, "E84.4.2", {"start": v(112.25, 27.07) * mm, "end": v(112.73, 25.65) * mm});
            skLineSegment(sketch, "E84.4.3", {"start": v(112.73, 25.65) * mm, "end": v(111.3, 25.17) * mm});
            skLineSegment(sketch, "E84.4.4", {"start": v(110.83, 26.6) * mm, "end": v(111.3, 25.17) * mm});
            skLineSegment(sketch, "E84.4.5", {"start": v(110.83, 26.6) * mm, "end": v(110.36, 28.02) * mm});
            skLineSegment(sketch, "E84.5.0", {"start": v(113.52, 20.9) * mm, "end": v(112.02, 20.89) * mm});
            skLineSegment(sketch, "E84.5.1", {"start": v(113.53, 19.4) * mm, "end": v(113.52, 20.9) * mm});
            skLineSegment(sketch, "E84.5.2", {"start": v(113.53, 19.4) * mm, "end": v(113.55, 17.9) * mm});
            skLineSegment(sketch, "E84.5.3", {"start": v(113.55, 17.9) * mm, "end": v(112.05, 17.89) * mm});
            skLineSegment(sketch, "E84.5.4", {"start": v(112.03, 19.39) * mm, "end": v(112.05, 17.89) * mm});
            skLineSegment(sketch, "E84.5.5", {"start": v(112.03, 19.39) * mm, "end": v(112.02, 20.89) * mm});
            skLineSegment(sketch, "E84.6.0", {"start": v(112.84, 13.14) * mm, "end": v(111.41, 13.59) * mm});
            skLineSegment(sketch, "E84.6.1", {"start": v(112.4, 11.7) * mm, "end": v(112.84, 13.14) * mm});
            skLineSegment(sketch, "E84.6.2", {"start": v(112.4, 11.7) * mm, "end": v(111.95, 10.28) * mm});
            skLineSegment(sketch, "E84.6.3", {"start": v(111.95, 10.28) * mm, "end": v(110.51, 10.72) * mm});
            skLineSegment(sketch, "E84.6.4", {"start": v(110.96, 12.15) * mm, "end": v(110.51, 10.72) * mm});
            skLineSegment(sketch, "E84.6.5", {"start": v(110.96, 12.15) * mm, "end": v(111.41, 13.59) * mm});
            skLineSegment(sketch, "E84.7.0", {"start": v(109.81, 5.96) * mm, "end": v(108.59, 6.83) * mm});
            skLineSegment(sketch, "E84.7.1", {"start": v(108.95, 4.74) * mm, "end": v(109.81, 5.96) * mm});
            skLineSegment(sketch, "E84.7.2", {"start": v(108.95, 4.74) * mm, "end": v(108.08, 3.51) * mm});
            skLineSegment(sketch, "E84.7.3", {"start": v(108.08, 3.51) * mm, "end": v(106.86, 4.38) * mm});
            skLineSegment(sketch, "E84.7.4", {"start": v(107.72, 5.6) * mm, "end": v(106.86, 4.38) * mm});
            skLineSegment(sketch, "E84.7.5", {"start": v(107.72, 5.6) * mm, "end": v(108.59, 6.83) * mm});
            skLineSegment(sketch, "E84.8.0", {"start": v(104.72, 0.06) * mm, "end": v(103.83, 1.26) * mm});
            skLineSegment(sketch, "E84.8.1", {"start": v(103.52, -0.84) * mm, "end": v(104.72, 0.06) * mm});
            skLineSegment(sketch, "E84.8.2", {"start": v(103.52, -0.84) * mm, "end": v(102.32, -1.74) * mm});
            skLineSegment(sketch, "E84.8.3", {"start": v(102.32, -1.74) * mm, "end": v(101.42, -0.54) * mm});
            skLineSegment(sketch, "E84.8.4", {"start": v(102.62, 0.36) * mm, "end": v(101.42, -0.54) * mm});
            skLineSegment(sketch, "E84.8.5", {"start": v(102.62, 0.36) * mm, "end": v(103.83, 1.26) * mm});
            skLineSegment(sketch, "E84.9.0", {"start": v(98.07, -3.99) * mm, "end": v(97.58, -2.57) * mm});
            skLineSegment(sketch, "E84.9.1", {"start": v(96.65, -4.48) * mm, "end": v(98.07, -3.99) * mm});
            skLineSegment(sketch, "E84.9.2", {"start": v(96.65, -4.48) * mm, "end": v(95.23, -4.96) * mm});
            skLineSegment(sketch, "E84.9.3", {"start": v(95.23, -4.96) * mm, "end": v(94.75, -3.54) * mm});
            skLineSegment(sketch, "E84.9.4", {"start": v(96.16, -3.06) * mm, "end": v(94.75, -3.54) * mm});
            skLineSegment(sketch, "E84.9.5", {"start": v(96.16, -3.06) * mm, "end": v(97.58, -2.57) * mm});
            skLineSegment(sketch, "E84.10.0", {"start": v(90.5, -5.8) * mm, "end": v(90.47, -4.3) * mm});
            skLineSegment(sketch, "E84.10.1", {"start": v(89, -5.83) * mm, "end": v(90.5, -5.8) * mm});
            skLineSegment(sketch, "E84.10.2", {"start": v(89, -5.83) * mm, "end": v(87.5, -5.85) * mm});
            skLineSegment(sketch, "E84.10.3", {"start": v(87.5, -5.85) * mm, "end": v(87.47, -4.35) * mm});
            skLineSegment(sketch, "E84.10.4", {"start": v(88.97, -4.33) * mm, "end": v(87.47, -4.35) * mm});
            skLineSegment(sketch, "E84.10.5", {"start": v(88.97, -4.33) * mm, "end": v(90.47, -4.3) * mm});
            skLineSegment(sketch, "E84.11.0", {"start": v(82.73, -5.2) * mm, "end": v(83.16, -3.76) * mm});
            skLineSegment(sketch, "E84.11.1", {"start": v(81.3, -4.76) * mm, "end": v(82.73, -5.2) * mm});
            skLineSegment(sketch, "E84.11.2", {"start": v(81.3, -4.76) * mm, "end": v(79.85, -4.32) * mm});
            skLineSegment(sketch, "E84.11.3", {"start": v(79.85, -4.32) * mm, "end": v(80.29, -2.89) * mm});
            skLineSegment(sketch, "E84.11.4", {"start": v(81.73, -3.32) * mm, "end": v(80.29, -2.89) * mm});
            skLineSegment(sketch, "E84.11.5", {"start": v(81.73, -3.32) * mm, "end": v(83.16, -3.76) * mm});
            skLineSegment(sketch, "E84.12.0", {"start": v(75.52, -2.23) * mm, "end": v(76.38, -1) * mm});
            skLineSegment(sketch, "E84.12.1", {"start": v(74.29, -1.37) * mm, "end": v(75.52, -2.23) * mm});
            skLineSegment(sketch, "E84.12.2", {"start": v(74.29, -1.37) * mm, "end": v(73.06, -0.52) * mm});
            skLineSegment(sketch, "E84.12.3", {"start": v(73.06, -0.52) * mm, "end": v(73.91, 0.71) * mm});
            skLineSegment(sketch, "E84.12.4", {"start": v(75.14, -0.14) * mm, "end": v(73.91, 0.71) * mm});
            skLineSegment(sketch, "E84.12.5", {"start": v(75.14, -0.14) * mm, "end": v(76.38, -1) * mm});
            skLineSegment(sketch, "E84.13.0", {"start": v(69.58, 2.8) * mm, "end": v(70.77, 3.71) * mm});
            skLineSegment(sketch, "E84.13.1", {"start": v(68.67, 4) * mm, "end": v(69.58, 2.8) * mm});
            skLineSegment(sketch, "E84.13.2", {"start": v(68.67, 4) * mm, "end": v(67.75, 5.19) * mm});
            skLineSegment(sketch, "E84.13.3", {"start": v(67.75, 5.19) * mm, "end": v(68.95, 6.1) * mm});
            skLineSegment(sketch, "E84.13.4", {"start": v(69.86, 4.9) * mm, "end": v(68.95, 6.1) * mm});
            skLineSegment(sketch, "E84.13.5", {"start": v(69.86, 4.9) * mm, "end": v(70.77, 3.71) * mm});
            skLineSegment(sketch, "E84.14.0", {"start": v(65.46, 9.42) * mm, "end": v(66.88, 9.92) * mm});
            skLineSegment(sketch, "E84.14.1", {"start": v(64.96, 10.84) * mm, "end": v(65.46, 9.42) * mm});
            skLineSegment(sketch, "E84.14.2", {"start": v(64.96, 10.84) * mm, "end": v(64.46, 12.25) * mm});
            skLineSegment(sketch, "E84.14.3", {"start": v(64.46, 12.25) * mm, "end": v(65.88, 12.75) * mm});
            skLineSegment(sketch, "E84.14.4", {"start": v(66.38, 11.34) * mm, "end": v(65.88, 12.75) * mm});
            skLineSegment(sketch, "E84.14.5", {"start": v(66.38, 11.34) * mm, "end": v(66.88, 9.92) * mm});
            skLineSegment(sketch, "E84.15.0", {"start": v(63.58, 16.98) * mm, "end": v(65.08, 17.02) * mm});
            skLineSegment(sketch, "E84.15.1", {"start": v(63.54, 18.48) * mm, "end": v(63.58, 16.98) * mm});
            skLineSegment(sketch, "E84.15.2", {"start": v(63.54, 18.48) * mm, "end": v(63.5, 19.98) * mm});
            skLineSegment(sketch, "E84.15.3", {"start": v(63.5, 19.98) * mm, "end": v(65, 20.02) * mm});
            skLineSegment(sketch, "E84.15.4", {"start": v(65.04, 18.52) * mm, "end": v(65, 20.02) * mm});
            skLineSegment(sketch, "E84.15.5", {"start": v(65.04, 18.52) * mm, "end": v(65.08, 17.02) * mm});
            skLineSegment(sketch, "E84.16.0", {"start": v(64.12, 24.75) * mm, "end": v(65.56, 24.33) * mm});
            skLineSegment(sketch, "E84.16.1", {"start": v(64.54, 26.2) * mm, "end": v(64.12, 24.75) * mm});
            skLineSegment(sketch, "E84.16.2", {"start": v(64.54, 26.2) * mm, "end": v(64.96, 27.63) * mm});
            skLineSegment(sketch, "E84.16.3", {"start": v(64.96, 27.63) * mm, "end": v(66.4, 27.21) * mm});
            skLineSegment(sketch, "E84.16.4", {"start": v(65.98, 25.77) * mm, "end": v(66.4, 27.21) * mm});
            skLineSegment(sketch, "E84.16.5", {"start": v(65.98, 25.77) * mm, "end": v(65.56, 24.33) * mm});
            skLineSegment(sketch, "E84.17.0", {"start": v(67.02, 31.99) * mm, "end": v(68.26, 31.14) * mm});
            skLineSegment(sketch, "E84.17.1", {"start": v(67.86, 33.23) * mm, "end": v(67.02, 31.99) * mm});
            skLineSegment(sketch, "E84.17.2", {"start": v(67.86, 33.23) * mm, "end": v(68.7, 34.47) * mm});
            skLineSegment(sketch, "E84.17.3", {"start": v(68.7, 34.47) * mm, "end": v(69.94, 33.62) * mm});
            skLineSegment(sketch, "E84.17.4", {"start": v(69.1, 32.38) * mm, "end": v(69.94, 33.62) * mm});
            skLineSegment(sketch, "E84.17.5", {"start": v(69.1, 32.38) * mm, "end": v(68.26, 31.14) * mm});
            skLineSegment(sketch, "E84.18.0", {"start": v(72, 37.98) * mm, "end": v(72.92, 36.8) * mm});
            skLineSegment(sketch, "E84.18.1", {"start": v(73.18, 38.9) * mm, "end": v(72, 37.98) * mm});
            skLineSegment(sketch, "E84.18.2", {"start": v(73.18, 38.9) * mm, "end": v(74.36, 39.82) * mm});
            skLineSegment(sketch, "E84.18.3", {"start": v(74.36, 39.82) * mm, "end": v(75.28, 38.64) * mm});
            skLineSegment(sketch, "E84.18.4", {"start": v(74.1, 37.71) * mm, "end": v(75.28, 38.64) * mm});
            skLineSegment(sketch, "E84.18.5", {"start": v(74.1, 37.71) * mm, "end": v(72.92, 36.8) * mm});
            skLineSegment(sketch, "E84.19.0", {"start": v(78.57, 42.15) * mm, "end": v(79.09, 40.74) * mm});
            skLineSegment(sketch, "E84.19.1", {"start": v(79.98, 42.66) * mm, "end": v(78.57, 42.15) * mm});
            skLineSegment(sketch, "E84.19.2", {"start": v(79.98, 42.66) * mm, "end": v(81.4, 43.18) * mm});
            skLineSegment(sketch, "E84.19.3", {"start": v(81.4, 43.18) * mm, "end": v(81.9, 41.77) * mm});
            skLineSegment(sketch, "E84.19.4", {"start": v(80.5, 41.25) * mm, "end": v(81.9, 41.77) * mm});
            skLineSegment(sketch, "E84.19.5", {"start": v(80.5, 41.25) * mm, "end": v(79.09, 40.74) * mm});
            skLineSegment(sketch, "E84.anchor1", {"start": v(88.53, 19.17) * mm, "end": v(87.03, 42.67) * mm, "construction": true});
            skLineSegment(sketch, "E84.anchor2", {"start": v(88.53, 19.17) * mm, "end": v(79.09, 40.74) * mm, "construction": true});
            skCircle(sketch, "E85", {"center": v(88.53, 19.17) * mm, "radius": 1.55 * mm});
            skCircle(sketch, "E86", {"center": v(88.53, 19.17) * mm, "radius": 5 * mm});
            skSolve(sketch);
        }
        {
            var Q0;
            {var subQ95=sQuery(id+"F27.wireOp",EDGE,"E80.top");Q0=makeQuery(id+"F27.imprint","IMPRINT",FACE,{"disambiguationData":[TD([[makeQuery(id+"F27.imprint","IMPRINT",EDGE,{"derivedFrom":subQ95}),-1.0]])]});}
            var Q1;
            {var subQ1=sQuery(id+"F21.wireOp",EDGE,"E35.0");var subQ2=makeQuery(id+"F22.opExtrude","SWEPT_FACE",FACE,{"disambiguationData":[OSD([subQ1])]});var subQ12=makeQuery(id+"F24.opExtrude","SWEPT_FACE",FACE,{"disambiguationData":[OSD([sQuery(id+"F23.wireOp",EDGE,"E75")])]});var subQ13=makeQuery(id+"F24.boolean.opBoolean","INTERSECT",EDGE,{"derivedFrom":[subQ2,subQ12]});var subQ17=sQuery(id+"F27.wireOp",EDGE,"E85");var subQ18=makeQuery(id+"F27.imprint","INTERSECT",VERTEX,{"derivedFrom":[subQ13,subQ17]});Q1=makeQuery(id+"F27.imprint","IMPRINT",FACE,{"disambiguationData":[TD([[makeQuery(id+"F27.imprint","IMPRINT",EDGE,{"disambiguationData":[TD([[subQ18,-1.0]])],"derivedFrom":subQ17}),-1.0]])]});}
            var Q2;
            {var subQ0=sQuery(id+"F27.wireOp",EDGE,"E86");var subQ1=sQuery(id+"F21.wireOp",EDGE,"E35.0");var subQ4=makeQuery(id+"F22.opExtrude","CAP_EDGE",EDGE,{"disambiguationData":[OSD([subQ1])],"isStart":true});var subQ16=makeQuery(id+"F27.imprint","INTERSECT",VERTEX,{"disambiguationData":[OD(0.0)],"derivedFrom":[subQ4,subQ0]});Q2=makeQuery(id+"F27.imprint","IMPRINT",FACE,{"disambiguationData":[TD([[makeQuery(id+"F27.imprint","IMPRINT",EDGE,{"disambiguationData":[TD([[subQ16,1.0]])],"derivedFrom":subQ4}),-1.0]])]});}
            var Q3;
            {var subQ0=sQuery(id+"F27.wireOp",EDGE,"E86");var subQ1=makeQuery(id+"F22.opExtrude","CAP_EDGE",EDGE,{"disambiguationData":[OSD([sQuery(id+"F21.wireOp",EDGE,"E35.0")])],"isStart":true});var subQ2=makeQuery(id+"F27.imprint","INTERSECT",VERTEX,{"disambiguationData":[OD(0.0)],"derivedFrom":[subQ1,subQ0]});Q3=makeQuery(id+"F27.imprint","IMPRINT",FACE,{"disambiguationData":[TD([[makeQuery(id+"F27.imprint","IMPRINT",EDGE,{"disambiguationData":[TD([[subQ2,-1.0]])],"derivedFrom":subQ0}),1.0]])]});}
            var Q4;
            {var subQ0=sQuery(id+"F27.wireOp",EDGE,"E84.15.4");Q4=makeQuery(id+"F27.imprint","IMPRINT",FACE,{"disambiguationData":[TD([[makeQuery(id+"F27.imprint","IMPRINT",EDGE,{"derivedFrom":subQ0}),-1.0]])]});}
            var Q5;
            {var subQ0=sQuery(id+"F27.wireOp",EDGE,"E86");var subQ1=sQuery(id+"F21.wireOp",EDGE,"E35.0");var subQ2=sQuery(id+"F21.wireOp",EDGE,"E23");var subQ5=makeQuery(id+"F22.opExtrude","SWEPT_EDGE",EDGE,{"disambiguationData":[OSD([subQ2,subQ1])]});var subQ6=makeQuery(id+"F27.imprint","INTERSECT",VERTEX,{"derivedFrom":[subQ5,subQ0]});Q5=makeQuery(id+"F27.imprint","IMPRINT",FACE,{"disambiguationData":[TD([[makeQuery(id+"F27.imprint","IMPRINT",EDGE,{"disambiguationData":[TD([[subQ6,-1.0]])],"derivedFrom":subQ0}),-1.0]])]});}
            var Q6;
            {var subQ0=sQuery(id+"F27.wireOp",EDGE,"E86");var subQ1=sQuery(id+"F21.wireOp",EDGE,"E35.0");var subQ4=makeQuery(id+"F22.opExtrude","CAP_EDGE",EDGE,{"disambiguationData":[OSD([subQ1])],"isStart":true});var subQ5=makeQuery(id+"F27.imprint","INTERSECT",VERTEX,{"disambiguationData":[OD(1.0)],"derivedFrom":[subQ4,subQ0]});Q6=makeQuery(id+"F27.imprint","IMPRINT",FACE,{"disambiguationData":[TD([[makeQuery(id+"F27.imprint","IMPRINT",EDGE,{"disambiguationData":[TD([[subQ5,-1.0]])],"derivedFrom":subQ0}),-1.0]])]});}
            extrude(context, id + "F28", {"entities" : qUnion([Q0, Q1, Q2, Q3, Q4, Q5, Q6]), "depth" : 6 * mm});
        }
    });
